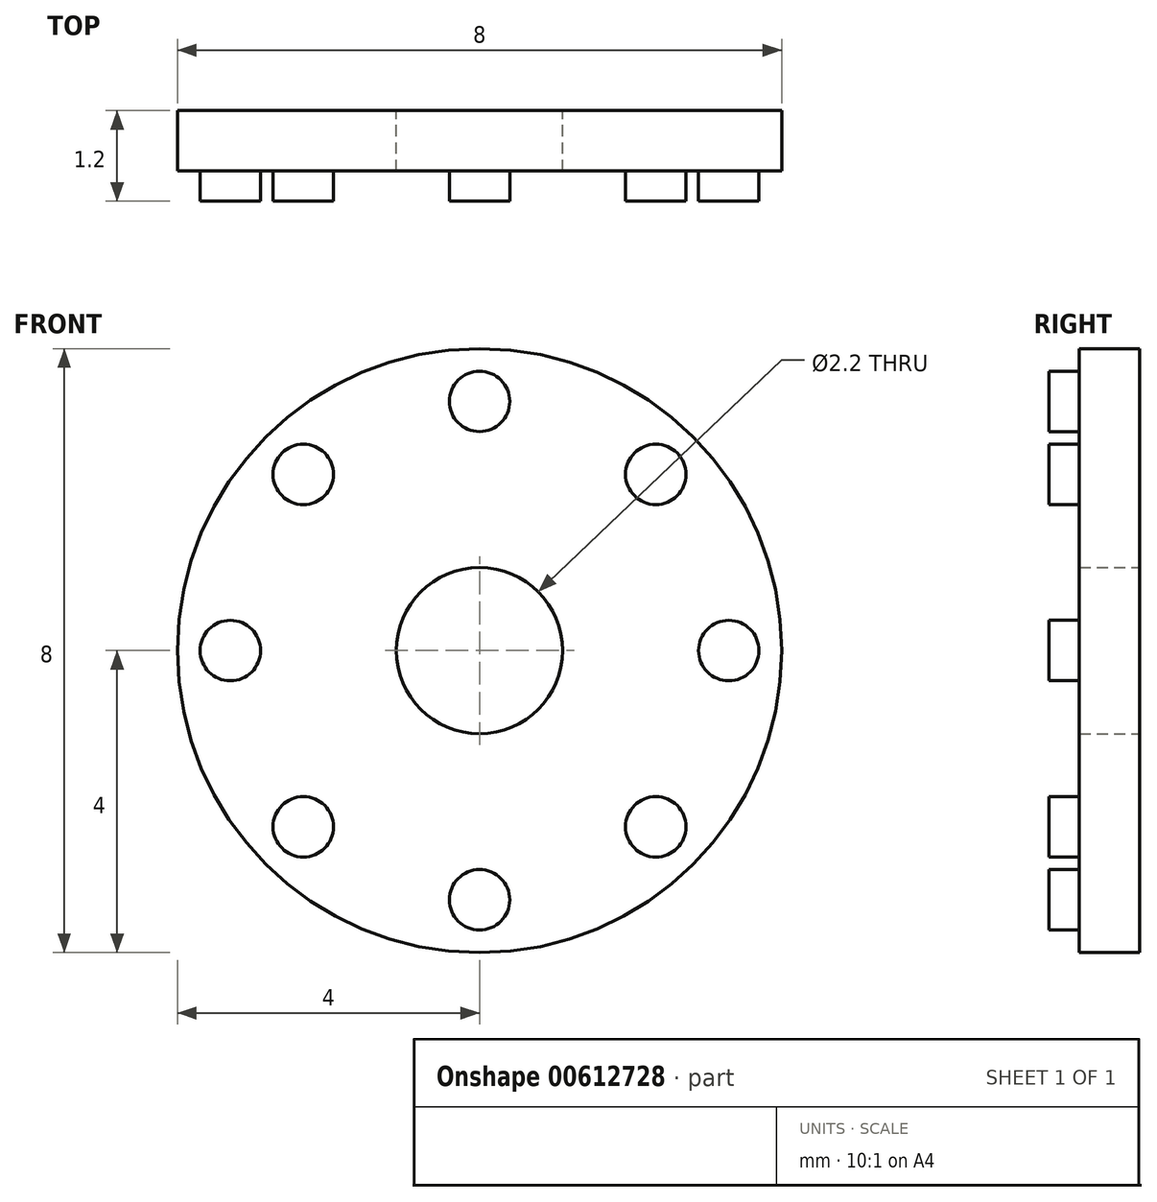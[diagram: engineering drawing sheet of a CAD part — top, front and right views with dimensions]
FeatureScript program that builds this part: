
annotation { "Feature Type Name" : "Feature", "Feature Type Description" : "" }
export const myFeature = defineFeature(function(context is Context, id is Id, definition is map)
    precondition{}
    {
        {
            var Q0;
            Q0=qCreatedBy(makeId("Front.planeOp"),FACE);
            var sketch = newSketch(context, id + "F0", { "sketchPlane" : qUnion([Q0])});
            skCircle(sketch, "E0", {"center": v(0, 0) * mm, "radius": 4 * mm});
            skCircle(sketch, "E1", {"center": v(0, 0) * mm, "radius": 1.1 * mm});
            skSolve(sketch);
        }
        {
            var Q0;
            Q0=qSketchRegion(id+"F0",true);
            extrude(context, id + "F1", {"entities" : qUnion([Q0]), "depth" : 0.8 * mm, "offsetDistance" : 25 * mm});
        }
        {
            var Q0;
            Q0=makeQuery(id+"F1.opExtrude","CAP_FACE",FACE,{"disambiguationData":[OSD([sQuery(id+"F0.wireOp",EDGE,"E0")])],"isStart":false});
            var sketch = newSketch(context, id + "F2", { "sketchPlane" : qUnion([Q0])});
            skCircle(sketch, "E2", {"center": v(0, 3.3) * mm, "radius": 0.4 * mm});
            skSolve(sketch);
        }
        {
            var Q0;
            Q0=qSketchRegion(id+"F2",true);
            extrude(context, id + "F3", {"entities" : qUnion([Q0]), "depth" : 0.4 * mm, "offsetDistance" : 25 * mm});
        }
        {
            var Q0;
            Q0=makeQuery(id+"F3.opExtrude","SWEPT_BODY",BODY,{"disambiguationData":[OSD([sQuery(id+"F2.wireOp",EDGE,"E2")])]});
            var Q1;
            Q1=makeQuery(id+"F1.opExtrude","CAP_EDGE",EDGE,{"disambiguationData":[OSD([sQuery(id+"F0.wireOp",EDGE,"E0")])],"isStart":false});
            circularPattern(context, id + "F4", {"entities" : qUnion([Q0]), "axis" : qUnion([Q1]), "angle" : 360 * degree, "instanceCount" : 8, "equalSpace" : true});
        }
    });
